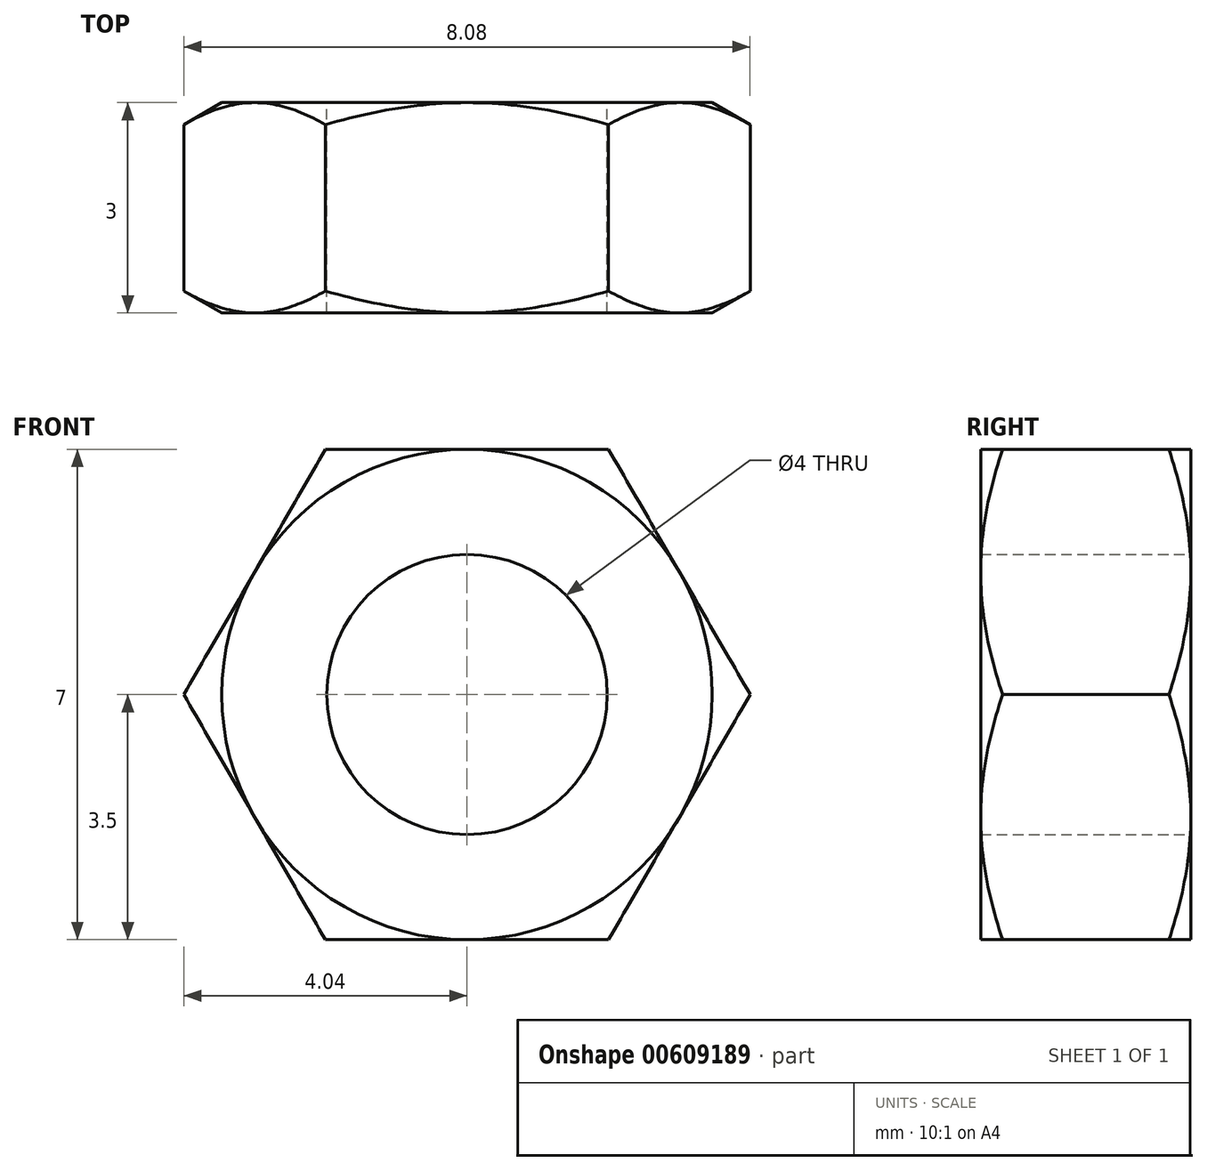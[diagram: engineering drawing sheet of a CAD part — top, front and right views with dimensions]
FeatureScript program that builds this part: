
annotation { "Feature Type Name" : "Feature", "Feature Type Description" : "" }
export const myFeature = defineFeature(function(context is Context, id is Id, definition is map)
    precondition{}
    {
        {
            var Q0;
            Q0=qCreatedBy(makeId("Front.planeOp"),FACE);
            var sketch = newSketch(context, id + "F0", { "sketchPlane" : qUnion([Q0])});
            skCircle(sketch, "E0", {"center": v(0, 0) * mm, "radius": 2 * mm});
            skCircle(sketch, "E1.cCircle", {"center": v(0, 0) * mm, "radius": 3.5 * mm, "construction": true});
            skLineSegment(sketch, "E1.0", {"start": v(-2.02, 3.5) * mm, "end": v(2.02, 3.5) * mm});
            skLineSegment(sketch, "E1.1", {"start": v(2.02, 3.5) * mm, "end": v(4.04, 0) * mm});
            skLineSegment(sketch, "E1.2", {"start": v(4.04, 0) * mm, "end": v(2.02, -3.5) * mm});
            skLineSegment(sketch, "E1.3", {"start": v(2.02, -3.5) * mm, "end": v(-2.02, -3.5) * mm});
            skLineSegment(sketch, "E1.4", {"start": v(-2.02, -3.5) * mm, "end": v(-4.04, 0) * mm});
            skLineSegment(sketch, "E1.5", {"start": v(-4.04, 0) * mm, "end": v(-2.02, 3.5) * mm});
            skPoint(sketch, "E1.0.midPoint", {"position": v(0, 3.5) * mm});
            skSolve(sketch);
        }
        {
            var Q0;
            Q0=qSketchRegion(id+"F0",true);
            extrude(context, id + "F1", {"entities" : qUnion([Q0]), "depth" : 3 * mm, "offsetDistance" : 25 * mm});
        }
        {
            var Q0;
            Q0=qCreatedBy(makeId("Right.planeOp"),FACE);
            var sketch = newSketch(context, id + "F2", { "sketchPlane" : qUnion([Q0])});
            skLineSegment(sketch, "E2", {"start": v(-0.46, 4.3) * mm, "end": v(0, 3.5) * mm});
            skLineSegment(sketch, "E3", {"start": v(-3, 4.3) * mm, "end": v(-3, 3.5) * mm});
            skLineSegment(sketch, "E4", {"start": v(-3, 3.5) * mm, "end": v(-2.54, 4.3) * mm});
            skLineSegment(sketch, "E5", {"start": v(-2.54, 4.3) * mm, "end": v(-3, 4.3) * mm});
            skLineSegment(sketch, "E6", {"start": v(0, 0) * mm, "end": v(-5.03, 0) * mm, "construction": true});
            skLineSegment(sketch, "E7", {"start": v(-0.46, 4.3) * mm, "end": v(0, 4.3) * mm});
            skLineSegment(sketch, "E8", {"start": v(0, 4.3) * mm, "end": v(0, 3.5) * mm});
            skSolve(sketch);
        }
        {
            var Q0;
            Q0=qSketchRegion(id+"F2",true);
            var Q1;
            Q1=sQuery(id+"F2.wireOp",EDGE,"E6");
            revolve(context, id + "F3", {"operationType" : NewBodyOperationType.REMOVE, "entities" : qUnion([Q0]), "axis" : qUnion([Q1]), "revolveType" : RevolveType.FULL, "oppositeDirection" : true});
        }
    });
